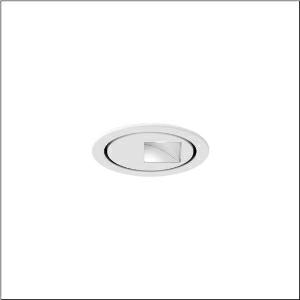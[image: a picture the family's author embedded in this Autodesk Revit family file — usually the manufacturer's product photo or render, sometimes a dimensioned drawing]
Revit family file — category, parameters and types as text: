
# Revit family: lunis_11_micro_round_51dj11b71wn21
name_source: partatom
category: Lighting Fixtures
units: mm (PartAtom-declared; Revit-internal decimal feet)

## family parameters
Cut with Voids When Loaded = No
Host = Face
Light Source = No
Part Type = Normal
Room Calculation Point = No
Round Connector Dimension = Use Diameter
Shared = No

## types (1)
- Lunis 11 micro round (1 x LED 4000K / CRI = 90 (unbekannt), 1210 lm, 4000K)
    Apparent Load = 20 VA
    CIE Flux Codes = 42 75 96 100 100
    Color Rendering = 90
    Color Temperature = 4000K
    Default Elevation = 1800 mm
    Description = Lunis 11 micro round, downlight, light control with wallwasher, of highly reflective aluminium, highly specular, light emission: direct distribution, LED rated luminous flux: 1.210lm, light colour: 940, with terminal, 3-pole, mains connection: 220..230V, AC, 50/60Hz, LED module, of aluminium, highly specular, white, diameter: 114mm, clamping range: 1..40mm, recessing ring, of plastic, traffic white (RAL 9016), protection rating (complete): IP20, insulation class (complete): insulation class II (safety insulation), certification: CE, permissible ambient temperature for indoor applications: 0..+35°C, packaging unit: 1 piece
    Height = 0 mm  [stored 0 ft]
    Lamp = 1 x LED 4000K / CRI >= 90 (unbekannt)
    Lamp Light Flux = 1210 lm
    Lamp count = 1
    Length = 114 mm
    Luminous efficacy = 61 lm/W
    Manufacturer = Siteco
    ModVariant = No
    Model = 51DJ11B71WN21
    Mounting Place = Ceiling
    Mounting Type = Recessed
    Number of Poles = 1
    OnlyDefault = Yes
    Power Factor = 1
    Product Name = Lunis 11 micro round
    Product group = downlight
    ProductGroupID = 400
    Protection Class = Protection class II
    Protection Degree = IP 20
    RLX_Detail_Level = 1
    RLX_Emergency_Light_Flux = 0 lm
    RLX_Emergency_Type = 0
    RLX_Emergency_Type_DB = No
    RlxData = <blob elided: 41005 chars, md5=0421070a>
    Socket = socket
    Standby Power = 0 W
    System Light Flux = 1210 lm
    System Power = 20 W
    Type Comments = Product without accessories
    Type Image = l_1004773.jpg
    URL = http://relux.com
    VarID = ---
    Voltage = 0 V
    Weight = 0.00 kg
    Width = 114 mm

note: [stored X ft] marks values corroborated as IEEE doubles in the binary element streams (Revit-internal decimal feet)

## geometry (parser evidence)
native form markers: Blend x4, Sweep x10
no freeform markers — native parametric forms only
